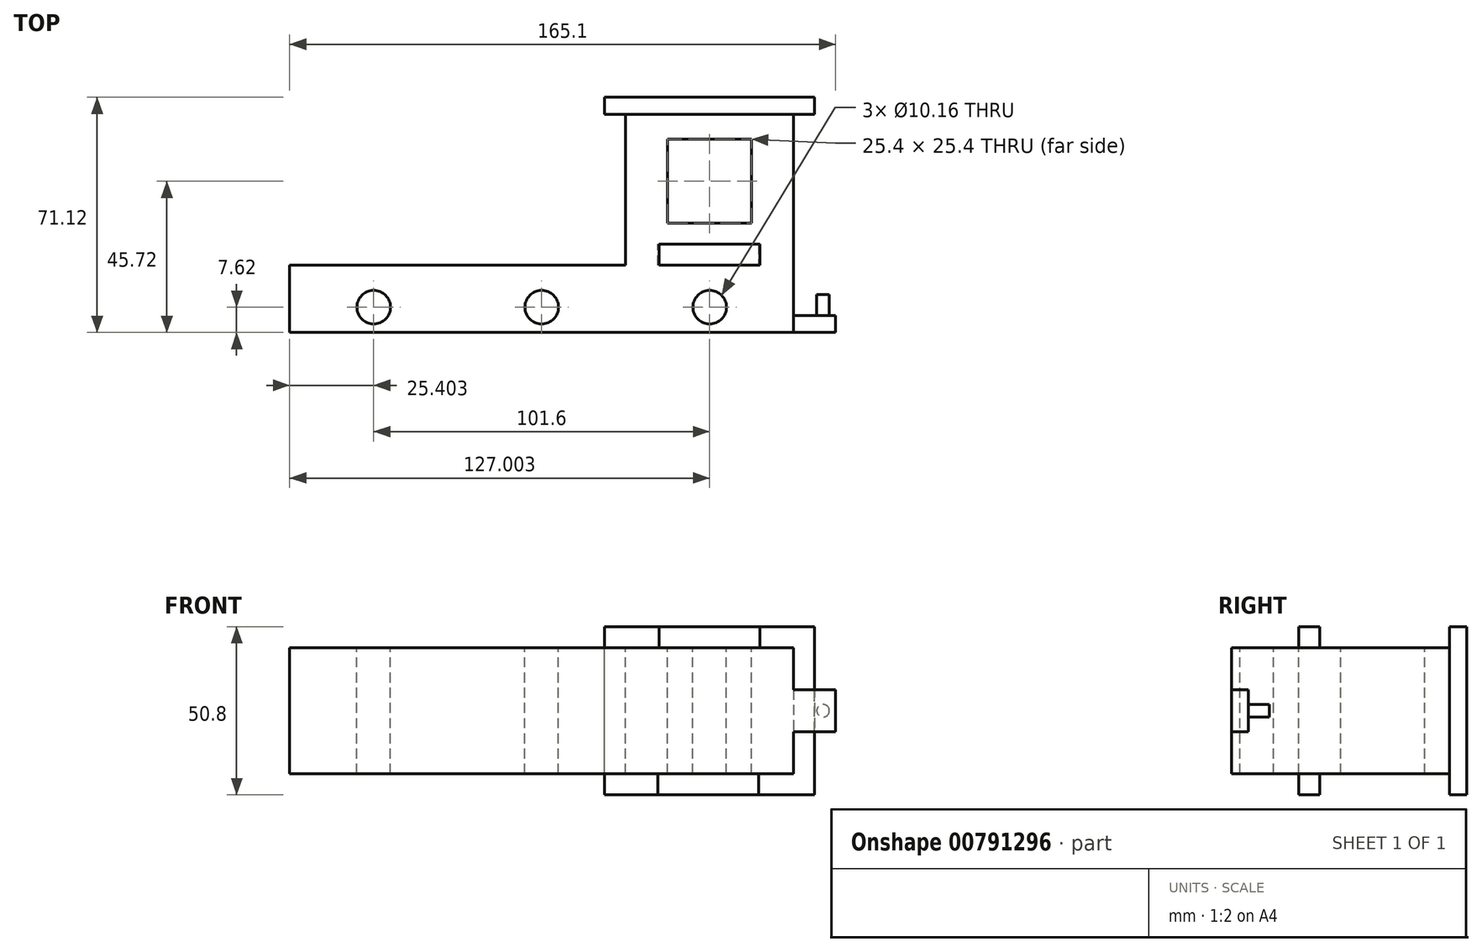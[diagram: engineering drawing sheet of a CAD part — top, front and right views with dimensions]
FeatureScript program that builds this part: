
annotation { "Feature Type Name" : "Feature", "Feature Type Description" : "" }
export const myFeature = defineFeature(function(context is Context, id is Id, definition is map)
    precondition{}
    {
        {
            var Q0;
            Q0=qCreatedBy(makeId("Front.planeOp"),FACE);
            var sketch = newSketch(context, id + "F0", { "sketchPlane" : qUnion([Q0])});
            skLineSegment(sketch, "E0.bottom", {"start": v(-68.46, 19.52) * mm, "end": v(83.94, 19.52) * mm});
            skLineSegment(sketch, "E0.top", {"start": v(-68.46, -18.58) * mm, "end": v(83.94, -18.58) * mm});
            skLineSegment(sketch, "E0.left", {"start": v(-68.46, 19.52) * mm, "end": v(-68.46, -18.58) * mm});
            skLineSegment(sketch, "E0.right", {"start": v(83.94, 19.52) * mm, "end": v(83.94, -18.58) * mm});
            skSolve(sketch);
        }
        {
            var Q0;
            Q0=qSketchRegion(id+"F0",true);
            extrude(context, id + "F1", {"entities" : qUnion([Q0]), "depth" : 20.32 * mm});
        }
        {
            var Q0;
            Q0=makeQuery(id+"F1.opExtrude","CAP_FACE",FACE,{"disambiguationData":[OSD([sQuery(id+"F0.wireOp",EDGE,"E0.bottom"),sQuery(id+"F0.wireOp",EDGE,"E0.top"),sQuery(id+"F0.wireOp",EDGE,"E0.left"),sQuery(id+"F0.wireOp",EDGE,"E0.right")])],"isStart":true});
            var sketch = newSketch(context, id + "F2", { "sketchPlane" : qUnion([Q0])});
            skLineSegment(sketch, "E1", {"start": v(-33.14, -18.58) * mm, "end": v(-33.14, 19.52) * mm});
            skSolve(sketch);
        }
        {
            var Q0;
            {var subQ0=sQuery(id+"F2.wireOp",EDGE,"E1");Q0=makeQuery(id+"F2.imprint","IMPRINT",FACE,{"disambiguationData":[TD([[makeQuery(id+"F2.imprint","IMPRINT",EDGE,{"derivedFrom":subQ0}),1.0]])]});}
            extrude(context, id + "F3", {"entities" : qUnion([Q0]), "operationType" : NewBodyOperationType.ADD, "depth" : 50.8 * mm});
        }
        {
            var Q0;
            {var subQ0=sQuery(id+"F0.wireOp",EDGE,"E0.bottom");Q0=makeQuery(id+"F3.boolean.opBoolean","MERGE",FACE,{"derivedFrom":[makeQuery(id+"F1.opExtrude","SWEPT_FACE",FACE,{"disambiguationData":[OSD([subQ0])]}),makeQuery(id+"F3.opExtrude","SWEPT_FACE",FACE,{"disambiguationData":[OSD([subQ0])]})]});}
            var sketch = newSketch(context, id + "F4", { "sketchPlane" : qUnion([Q0])});
            skLineSegment(sketch, "E2.bottom", {"start": v(45.84, 38.1) * mm, "end": v(71.24, 38.1) * mm});
            skLineSegment(sketch, "E2.top", {"start": v(45.84, 12.7) * mm, "end": v(71.24, 12.7) * mm});
            skLineSegment(sketch, "E2.left", {"start": v(45.84, 38.1) * mm, "end": v(45.84, 12.7) * mm});
            skLineSegment(sketch, "E2.right", {"start": v(71.24, 38.1) * mm, "end": v(71.24, 12.7) * mm});
            skSolve(sketch);
        }
        {
            var Q0;
            Q0=qSketchRegion(id+"F4",true);
            extrude(context, id + "F5", {"entities" : qUnion([Q0]), "operationType" : NewBodyOperationType.REMOVE, "endBound" : BoundingType.THROUGH_ALL, "oppositeDirection" : true, "depth" : 25.4 * mm});
        }
        {
            var Q0;
            {var subQ0=sQuery(id+"F0.wireOp",EDGE,"E0.bottom");Q0=makeQuery(id+"F3.boolean.opBoolean","MERGE",FACE,{"derivedFrom":[makeQuery(id+"F1.opExtrude","SWEPT_FACE",FACE,{"disambiguationData":[OSD([subQ0])]}),makeQuery(id+"F3.opExtrude","SWEPT_FACE",FACE,{"disambiguationData":[OSD([subQ0])]})]});}
            var sketch = newSketch(context, id + "F6", { "sketchPlane" : qUnion([Q0])});
            skLineSegment(sketch, "E3.top", {"start": v(43.3, 0) * mm, "end": v(73.78, 0) * mm});
            skLineSegment(sketch, "E4.MirrorCS", {"start": v(43.3, 6.35) * mm, "end": v(73.78, 6.35) * mm});
            skLineSegment(sketch, "E5.MirrorCS", {"start": v(43.3, 6.35) * mm, "end": v(43.3, 0) * mm});
            skLineSegment(sketch, "E6.MirrorCS", {"start": v(73.78, 6.35) * mm, "end": v(73.78, 0) * mm});
            skLineSegment(sketch, "E7", {"start": v(73.78, 0) * mm, "end": v(43.3, 0) * mm});
            skSolve(sketch);
        }
        {
            var Q0;
            Q0=qSketchRegion(id+"F6",true);
            extrude(context, id + "F7", {"entities" : qUnion([Q0]), "operationType" : NewBodyOperationType.ADD, "depth" : 6.35 * mm});
        }
        {
            var Q0;
            {var subQ0=sQuery(id+"F0.wireOp",EDGE,"E0.top");Q0=makeQuery(id+"F3.boolean.opBoolean","MERGE",FACE,{"derivedFrom":[makeQuery(id+"F1.opExtrude","SWEPT_FACE",FACE,{"disambiguationData":[OSD([subQ0])]}),makeQuery(id+"F3.opExtrude","SWEPT_FACE",FACE,{"disambiguationData":[OSD([subQ0])]})]});}
            var sketch = newSketch(context, id + "F8", { "sketchPlane" : qUnion([Q0])});
            skLineSegment(sketch, "E8.MirrorCS", {"start": v(42.87, -6.35) * mm, "end": v(73.35, -6.35) * mm});
            skLineSegment(sketch, "E9.MirrorCS", {"start": v(42.87, 0) * mm, "end": v(42.87, -6.35) * mm});
            skLineSegment(sketch, "E10.MirrorCS", {"start": v(73.35, -6.35) * mm, "end": v(73.35, 0) * mm});
            skLineSegment(sketch, "E11", {"start": v(73.35, 0) * mm, "end": v(42.87, 0) * mm});
            skSolve(sketch);
        }
        {
            var Q0;
            Q0=qSketchRegion(id+"F8",true);
            extrude(context, id + "F9", {"entities" : qUnion([Q0]), "operationType" : NewBodyOperationType.ADD, "depth" : 6.35 * mm});
        }
        {
            var Q0;
            {var subQ0=sQuery(id+"F0.wireOp",EDGE,"E0.right");Q0=makeQuery(id+"F3.boolean.opBoolean","MERGE",FACE,{"derivedFrom":[makeQuery(id+"F1.opExtrude","SWEPT_FACE",FACE,{"disambiguationData":[OSD([subQ0])]}),makeQuery(id+"F3.opExtrude","SWEPT_FACE",FACE,{"disambiguationData":[OSD([subQ0])]})]});}
            var sketch = newSketch(context, id + "F10", { "sketchPlane" : qUnion([Q0])});
            skLineSegment(sketch, "E12", {"start": v(45.65, -18.58) * mm, "end": v(45.65, 19.52) * mm});
            skSolve(sketch);
        }
        {
            var Q0;
            {var subQ0=sQuery(id+"F10.wireOp",EDGE,"E12");Q0=makeQuery(id+"F10.imprint","IMPRINT",FACE,{"disambiguationData":[TD([[makeQuery(id+"F10.imprint","IMPRINT",EDGE,{"derivedFrom":subQ0}),-1.0]])]});}
            extrude(context, id + "F11", {"entities" : qUnion([Q0]), "operationType" : NewBodyOperationType.ADD, "depth" : 6.35 * mm});
        }
        {
            var Q0;
            Q0=makeQuery(id+"F6.imprint","IMPRINT",FACE,{"disambiguationData":[TD([[makeQuery(id+"F6.imprint","IMPRINT",EDGE,{"derivedFrom":sQuery(id+"F6.wireOp",EDGE,"E4.MirrorCS")}),1.0]])]});
            var sketch = newSketch(context, id + "F12", { "sketchPlane" : qUnion([Q0])});
            skLineSegment(sketch, "E13", {"start": v(83.94, 45.65) * mm, "end": v(33.14, 45.65) * mm});
            skSolve(sketch);
        }
        {
            var Q0;
            {var subQ0=sQuery(id+"F12.wireOp",EDGE,"E13");Q0=makeQuery(id+"F12.imprint","IMPRINT",FACE,{"disambiguationData":[TD([[makeQuery(id+"F12.imprint","IMPRINT",EDGE,{"derivedFrom":subQ0}),-1.0]])]});}
            extrude(context, id + "F13", {"entities" : qUnion([Q0]), "operationType" : NewBodyOperationType.ADD, "depth" : 6.35 * mm});
        }
        {
            var Q0;
            Q0=makeQuery(id+"F13.opExtrude","SWEPT_FACE",FACE,{"disambiguationData":[OSD([sQuery(id+"F0.wireOp",EDGE,"E0.bottom"),sQuery(id+"F0.wireOp",EDGE,"E0.right")])]});
            extrude(context, id + "F14", {"entities" : qUnion([Q0]), "operationType" : NewBodyOperationType.ADD, "depth" : 6.35 * mm});
        }
        {
            var Q0;
            {var subQ0=sQuery(id+"F0.wireOp",EDGE,"E0.top");Q0=makeQuery(id+"F11.boolean.opBoolean","MERGE",FACE,{"derivedFrom":[makeQuery(id+"F3.boolean.opBoolean","MERGE",FACE,{"derivedFrom":[makeQuery(id+"F1.opExtrude","SWEPT_FACE",FACE,{"disambiguationData":[OSD([subQ0])]}),makeQuery(id+"F3.opExtrude","SWEPT_FACE",FACE,{"disambiguationData":[OSD([subQ0])]})]}),makeQuery(id+"F11.opExtrude","SWEPT_FACE",FACE,{"disambiguationData":[OSD([subQ0,sQuery(id+"F0.wireOp",EDGE,"E0.right")])]})]});}
            var sketch = newSketch(context, id + "F15", { "sketchPlane" : qUnion([Q0])});
            skLineSegment(sketch, "E14", {"start": v(83.94, -45.65) * mm, "end": v(33.14, -45.65) * mm});
            skSolve(sketch);
        }
        {
            var Q0;
            {var subQ3=sQuery(id+"F15.wireOp",EDGE,"E14");Q0=makeQuery(id+"F15.imprint","IMPRINT",FACE,{"disambiguationData":[TD([[makeQuery(id+"F15.imprint","IMPRINT",EDGE,{"derivedFrom":subQ3}),1.0]])]});}
            extrude(context, id + "F16", {"entities" : qUnion([Q0]), "operationType" : NewBodyOperationType.ADD, "depth" : 6.35 * mm});
        }
        {
            var Q0;
            {var subQ0=sQuery(id+"F2.wireOp",EDGE,"E1");Q0=makeQuery(id+"F16.boolean.opBoolean","MERGE",FACE,{"derivedFrom":[makeQuery(id+"F13.boolean.opBoolean","MERGE",FACE,{"derivedFrom":[makeQuery(id+"F3.opExtrude","SWEPT_FACE",FACE,{"disambiguationData":[OSD([subQ0])]}),makeQuery(id+"F13.opExtrude","SWEPT_FACE",FACE,{"disambiguationData":[OSD([sQuery(id+"F0.wireOp",EDGE,"E0.bottom"),subQ0])]})]}),makeQuery(id+"F16.opExtrude","SWEPT_FACE",FACE,{"disambiguationData":[OSD([sQuery(id+"F0.wireOp",EDGE,"E0.top"),subQ0])]})]});}
            var sketch = newSketch(context, id + "F17", { "sketchPlane" : qUnion([Q0])});
            skLineSegment(sketch, "E15", {"start": v(-45.65, -18.58) * mm, "end": v(-45.65, 19.52) * mm});
            skSolve(sketch);
        }
        {
            var Q0;
            Q0=makeQuery(id+"F17.imprint","IMPRINT",FACE,{"disambiguationData":[TD([[makeQuery(id+"F17.imprint","IMPRINT",EDGE,{"derivedFrom":sQuery(id+"F17.wireOp",EDGE,"E15")}),1.0]])]});
            extrude(context, id + "F18", {"entities" : qUnion([Q0]), "operationType" : NewBodyOperationType.ADD, "depth" : 6.35 * mm});
        }
        {
            var Q0;
            Q0=makeQuery(id+"F6.imprint","IMPRINT",FACE,{"disambiguationData":[TD([[makeQuery(id+"F6.imprint","IMPRINT",EDGE,{"derivedFrom":sQuery(id+"F6.wireOp",EDGE,"E4.MirrorCS")}),1.0]])]});
            var sketch = newSketch(context, id + "F19", { "sketchPlane" : qUnion([Q0])});
            skCircle(sketch, "E16", {"center": v(-43.06, -12.7) * mm, "radius": 5.08 * mm});
            skCircle(sketch, "E17", {"center": v(7.74, -12.7) * mm, "radius": 5.08 * mm});
            skCircle(sketch, "E18", {"center": v(58.54, -12.7) * mm, "radius": 5.08 * mm});
            skSolve(sketch);
        }
        {
            var Q0;
            Q0=qSketchRegion(id+"F19",true);
            extrude(context, id + "F20", {"entities" : qUnion([Q0]), "operationType" : NewBodyOperationType.REMOVE, "endBound" : BoundingType.THROUGH_ALL, "oppositeDirection" : true, "depth" : 25.4 * mm});
        }
        {
            var Q0;
            {var subQ0=sQuery(id+"F0.wireOp",EDGE,"E0.right");Q0=makeQuery(id+"F3.boolean.opBoolean","MERGE",FACE,{"derivedFrom":[makeQuery(id+"F1.opExtrude","SWEPT_FACE",FACE,{"disambiguationData":[OSD([subQ0])]}),makeQuery(id+"F3.opExtrude","SWEPT_FACE",FACE,{"disambiguationData":[OSD([subQ0])]})]});}
            var sketch = newSketch(context, id + "F21", { "sketchPlane" : qUnion([Q0])});
            skLineSegment(sketch, "E19.bottom", {"start": v(-15.24, 6.82) * mm, "end": v(-20.32, 6.82) * mm});
            skLineSegment(sketch, "E19.top", {"start": v(-15.24, -5.88) * mm, "end": v(-20.32, -5.88) * mm});
            skLineSegment(sketch, "E19.left", {"start": v(-15.24, 6.82) * mm, "end": v(-15.24, -5.88) * mm});
            skLineSegment(sketch, "E19.right", {"start": v(-20.32, 6.82) * mm, "end": v(-20.32, -5.88) * mm});
            skSolve(sketch);
        }
        {
            var Q0;
            Q0=makeQuery(id+"F21.imprint","IMPRINT",FACE,{"disambiguationData":[TD([[makeQuery(id+"F21.imprint","IMPRINT",EDGE,{"derivedFrom":sQuery(id+"F21.wireOp",EDGE,"E19.bottom")}),1.0]])]});
            extrude(context, id + "F22", {"entities" : qUnion([Q0]), "operationType" : NewBodyOperationType.ADD, "depth" : 12.7 * mm});
        }
        {
            var Q0;
            Q0=makeQuery(id+"F22.opExtrude","SWEPT_FACE",FACE,{"disambiguationData":[OSD([sQuery(id+"F21.wireOp",EDGE,"E19.left")])]});
            var sketch = newSketch(context, id + "F23", { "sketchPlane" : qUnion([Q0])});
            skCircle(sketch, "E20", {"center": v(-92.83, 0.47) * mm, "radius": 1.9 * mm});
            skSolve(sketch);
        }
        {
            var Q0;
            Q0=qSketchRegion(id+"F23",true);
            extrude(context, id + "F24", {"entities" : qUnion([Q0]), "operationType" : NewBodyOperationType.ADD, "depth" : 6.35 * mm});
        }
    });
